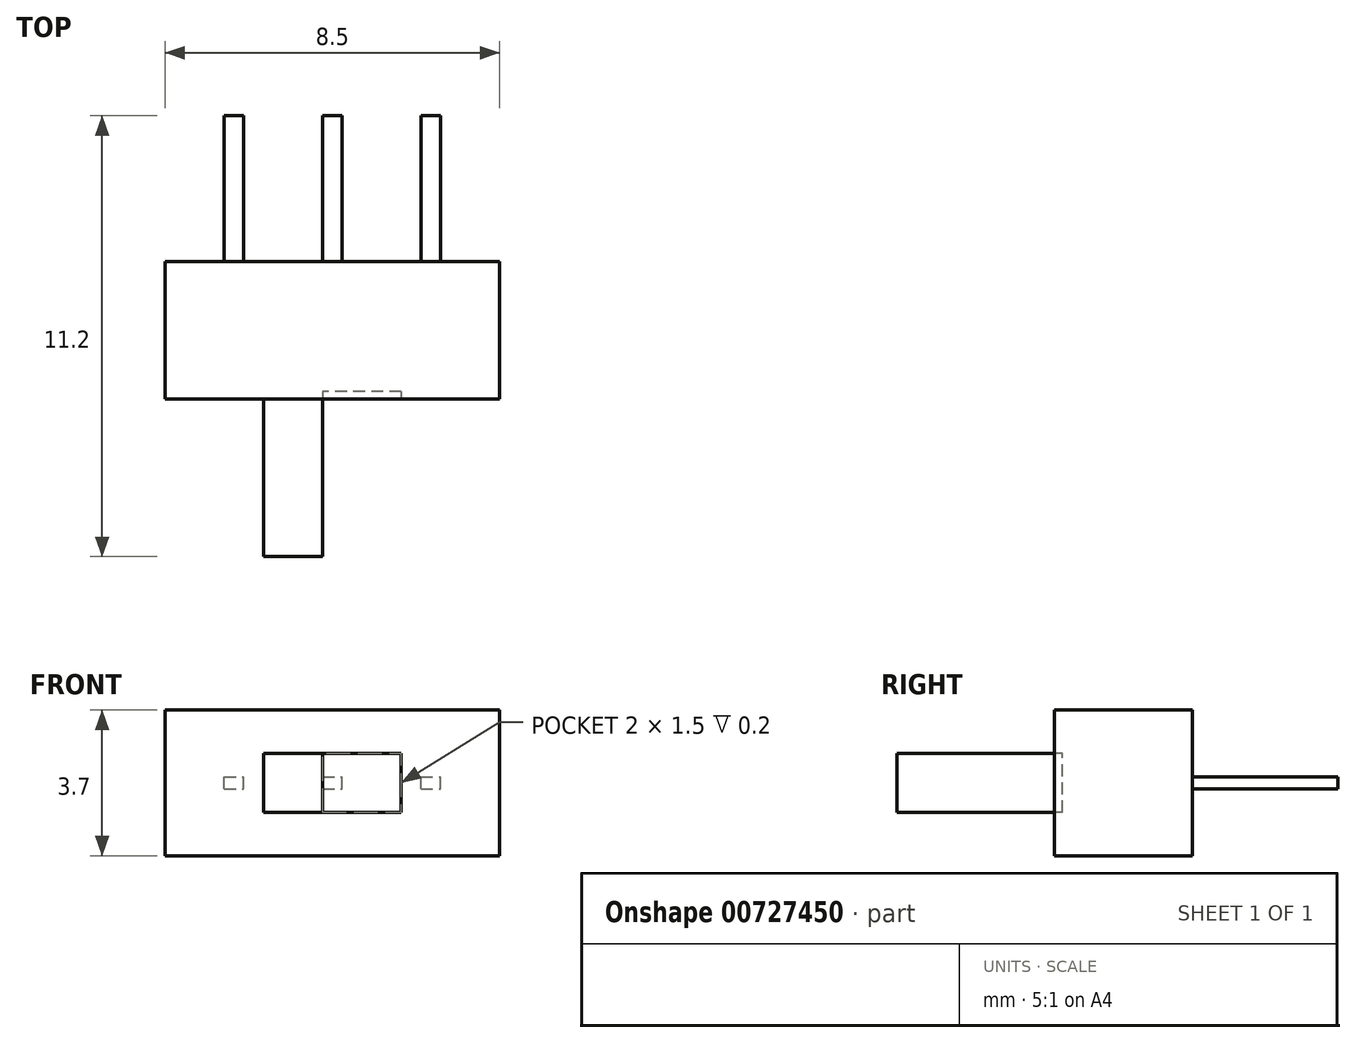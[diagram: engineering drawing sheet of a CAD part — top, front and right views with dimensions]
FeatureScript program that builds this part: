
annotation { "Feature Type Name" : "Feature", "Feature Type Description" : "" }
export const myFeature = defineFeature(function(context is Context, id is Id, definition is map)
    precondition{}
    {
        {
            var Q0;
            Q0=qCreatedBy(makeId("Front.planeOp"),FACE);
            var sketch = newSketch(context, id + "F0", { "sketchPlane" : qUnion([Q0])});
            skLineSegment(sketch, "E0.bottom", {"start": v(4.25, -1.85) * mm, "end": v(-4.25, -1.85) * mm});
            skLineSegment(sketch, "E0.top", {"start": v(4.25, 1.85) * mm, "end": v(-4.25, 1.85) * mm});
            skLineSegment(sketch, "E0.left", {"start": v(4.25, -1.85) * mm, "end": v(4.25, 1.85) * mm});
            skLineSegment(sketch, "E0.right", {"start": v(-4.25, -1.85) * mm, "end": v(-4.25, 1.85) * mm});
            skPoint(sketch, "E0.middle", {"position": v(0, 0) * mm});
            skSolve(sketch);
        }
        {
            var Q0;
            Q0 = qSketchRegion(id + "F0", true);
            extrude(context, id + "F1", {"entities" : qUnion([Q0]), "depth" : 3.5 * mm, "offsetDistance" : 25 * mm, "symmetric" : true});
        }
        {
            var Q0;
            Q0=makeQuery(id+"F1.opExtrude","CAP_FACE",FACE,{"disambiguationData":[OSD([sQuery(id+"F0.wireOp",EDGE,"E0.bottom"),sQuery(id+"F0.wireOp",EDGE,"E0.top"),sQuery(id+"F0.wireOp",EDGE,"E0.left"),sQuery(id+"F0.wireOp",EDGE,"E0.right")])],"isStart":true});
            var sketch = newSketch(context, id + "F2", { "sketchPlane" : qUnion([Q0])});
            skLineSegment(sketch, "E1.bottom", {"start": v(0.25, -0.15) * mm, "end": v(-0.25, -0.15) * mm});
            skLineSegment(sketch, "E1.top", {"start": v(0.25, 0.15) * mm, "end": v(-0.25, 0.15) * mm});
            skLineSegment(sketch, "E1.left", {"start": v(0.25, -0.15) * mm, "end": v(0.25, 0.15) * mm});
            skLineSegment(sketch, "E1.right", {"start": v(-0.25, -0.15) * mm, "end": v(-0.25, 0.15) * mm});
            skPoint(sketch, "E1.middle", {"position": v(0, 0) * mm});
            skLineSegment(sketch, "E2.bottom", {"start": v(2.75, -0.15) * mm, "end": v(2.25, -0.15) * mm});
            skLineSegment(sketch, "E2.top", {"start": v(2.75, 0.15) * mm, "end": v(2.25, 0.15) * mm});
            skLineSegment(sketch, "E2.left", {"start": v(2.75, -0.15) * mm, "end": v(2.75, 0.15) * mm});
            skLineSegment(sketch, "E2.right", {"start": v(2.25, -0.15) * mm, "end": v(2.25, 0.15) * mm});
            skPoint(sketch, "E2.middle", {"position": v(2.5, 0) * mm});
            skLineSegment(sketch, "E3.bottom", {"start": v(-2.25, -0.15) * mm, "end": v(-2.75, -0.15) * mm});
            skLineSegment(sketch, "E3.top", {"start": v(-2.25, 0.15) * mm, "end": v(-2.75, 0.15) * mm});
            skLineSegment(sketch, "E3.left", {"start": v(-2.25, -0.15) * mm, "end": v(-2.25, 0.15) * mm});
            skLineSegment(sketch, "E3.right", {"start": v(-2.75, -0.15) * mm, "end": v(-2.75, 0.15) * mm});
            skPoint(sketch, "E3.middle", {"position": v(-2.5, 0) * mm});
            skSolve(sketch);
        }
        {
            var Q0;
            Q0 = qSketchRegion(id + "F2", true);
            extrude(context, id + "F3", {"entities" : qUnion([Q0]), "operationType" : NewBodyOperationType.ADD, "depth" : 3.7 * mm, "offsetDistance" : 25 * mm});
        }
        {
            var Q0;
            Q0=makeQuery(id+"F1.opExtrude","CAP_FACE",FACE,{"disambiguationData":[OSD([sQuery(id+"F0.wireOp",EDGE,"E0.bottom"),sQuery(id+"F0.wireOp",EDGE,"E0.top"),sQuery(id+"F0.wireOp",EDGE,"E0.left"),sQuery(id+"F0.wireOp",EDGE,"E0.right")])],"isStart":false});
            var sketch = newSketch(context, id + "F4", { "sketchPlane" : qUnion([Q0])});
            skLineSegment(sketch, "E4.bottom", {"start": v(1.75, -0.75) * mm, "end": v(-1.75, -0.75) * mm});
            skLineSegment(sketch, "E4.top", {"start": v(1.75, 0.75) * mm, "end": v(-1.75, 0.75) * mm});
            skLineSegment(sketch, "E4.left", {"start": v(1.75, -0.75) * mm, "end": v(1.75, 0.75) * mm});
            skLineSegment(sketch, "E4.right", {"start": v(-1.75, -0.75) * mm, "end": v(-1.75, 0.75) * mm});
            skPoint(sketch, "E4.middle", {"position": v(0, 0) * mm});
            skLineSegment(sketch, "E5", {"start": v(-0.25, 0.75) * mm, "end": v(-0.25, -0.75) * mm});
            skSolve(sketch);
        }
        {
            var Q0;
            {var subQ0=sQuery(id+"F4.wireOp",EDGE,"E4.left");Q0=makeQuery(id+"F4.imprint","IMPRINT",FACE,{"disambiguationData":[TD([[makeQuery(id+"F4.imprint","IMPRINT",EDGE,{"derivedFrom":subQ0}),1.0]])]});}
            extrude(context, id + "F5", {"entities" : qUnion([Q0]), "operationType" : NewBodyOperationType.REMOVE, "oppositeDirection" : true, "depth" : 0.2 * mm, "offsetDistance" : 25 * mm});
        }
        {
            var Q0;
            {var subQ0=sQuery(id+"F4.wireOp",EDGE,"E4.right");Q0=makeQuery(id+"F4.imprint","IMPRINT",FACE,{"disambiguationData":[TD([[makeQuery(id+"F4.imprint","IMPRINT",EDGE,{"derivedFrom":subQ0}),-1.0]])]});}
            extrude(context, id + "F6", {"entities" : qUnion([Q0]), "operationType" : NewBodyOperationType.ADD, "depth" : 4 * mm, "offsetDistance" : 25 * mm});
        }
    });
